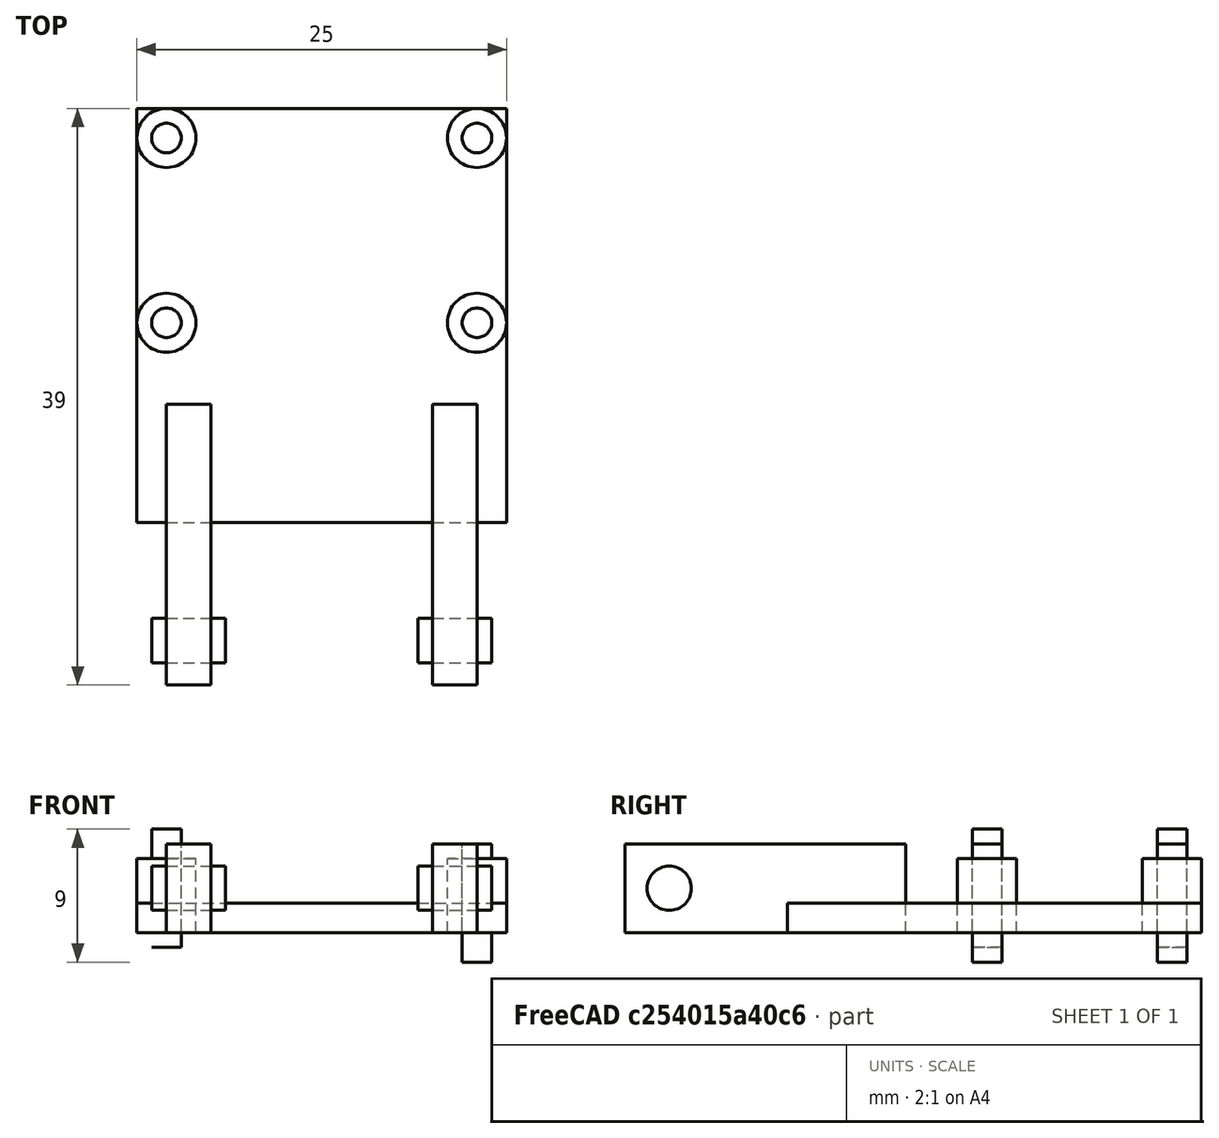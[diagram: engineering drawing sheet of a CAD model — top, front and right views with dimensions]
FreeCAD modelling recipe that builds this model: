
FCSTD DOCUMENT  (FreeCAD 0.16R6700 (Git))
Label: Camera hold Uncut
License: All rights reserved
LicenseURL: http://en.wikipedia.org/wiki/All_rights_reserved
objects: Part::Cylinder×10, Part::Box×3
note: 13 computed .brp shape members not serialized (recipe doc carries the construction recipe); baked Part::Feature solids carry a one-line shape summary decoded from their .brp

FEATURE [Part::Box] Box  label="Cube"
  Height = 2
  Length = 25
  Placement = pos=(0,-4,0) rot=(0,0,1;0rad)
  Width = 28
FEATURE [Part::Cylinder] Cylinder
  Angle = 360
  Height = 5
  Placement = pos=(2,9.5,0) rot=(0,0,1;0rad)
  Radius = 2
FEATURE [Part::Cylinder] Cylinder001
  Angle = 360
  Height = 5
  Placement = pos=(2,22,0) rot=(0,0,1;0rad)
  Radius = 2
FEATURE [Part::Cylinder] Cylinder002
  Angle = 360
  Height = 5
  Placement = pos=(23,22,0) rot=(0,0,1;0rad)
  Radius = 2
FEATURE [Part::Cylinder] Cylinder003
  Angle = 360
  Height = 5
  Placement = pos=(23,9.5,0) rot=(0,0,1;0rad)
  Radius = 2
FEATURE [Part::Cylinder] Cylinder004
  Angle = 360
  Height = 8
  Placement = pos=(2,9.5,-1) rot=(0,0,1;0rad)
  Radius = 1
FEATURE [Part::Cylinder] Cylinder005
  Angle = 360
  Height = 8
  Placement = pos=(2,22,-1) rot=(0,0,1;0rad)
  Radius = 1
FEATURE [Part::Cylinder] Cylinder006
  Angle = 360
  Height = 8
  Placement = pos=(23,22,-2) rot=(0,0,1;0rad)
  Radius = 1
FEATURE [Part::Cylinder] Cylinder007
  Angle = 360
  Height = 8
  Placement = pos=(23,9.5,-2) rot=(0,0,1;0rad)
  Radius = 1
FEATURE [Part::Box] Box001  label="Cube001"
  Height = 6
  Length = 3
  Placement = pos=(20,-15,0) rot=(0,0,1;0rad)
  Width = 19
FEATURE [Part::Box] Box002  label="Cube002"
  Height = 6
  Length = 3
  Placement = pos=(2,-15,0) rot=(0,0,1;0rad)
  Width = 19
FEATURE [Part::Cylinder] Cylinder008
  Angle = 360
  Height = 5
  Placement = pos=(19,-12,3) rot=(0,1,0;1.5708rad)
  Radius = 1.5
FEATURE [Part::Cylinder] Cylinder009
  Angle = 360
  Height = 5
  Placement = pos=(1,-12,3) rot=(0,1,0;1.5708rad)
  Radius = 1.5
